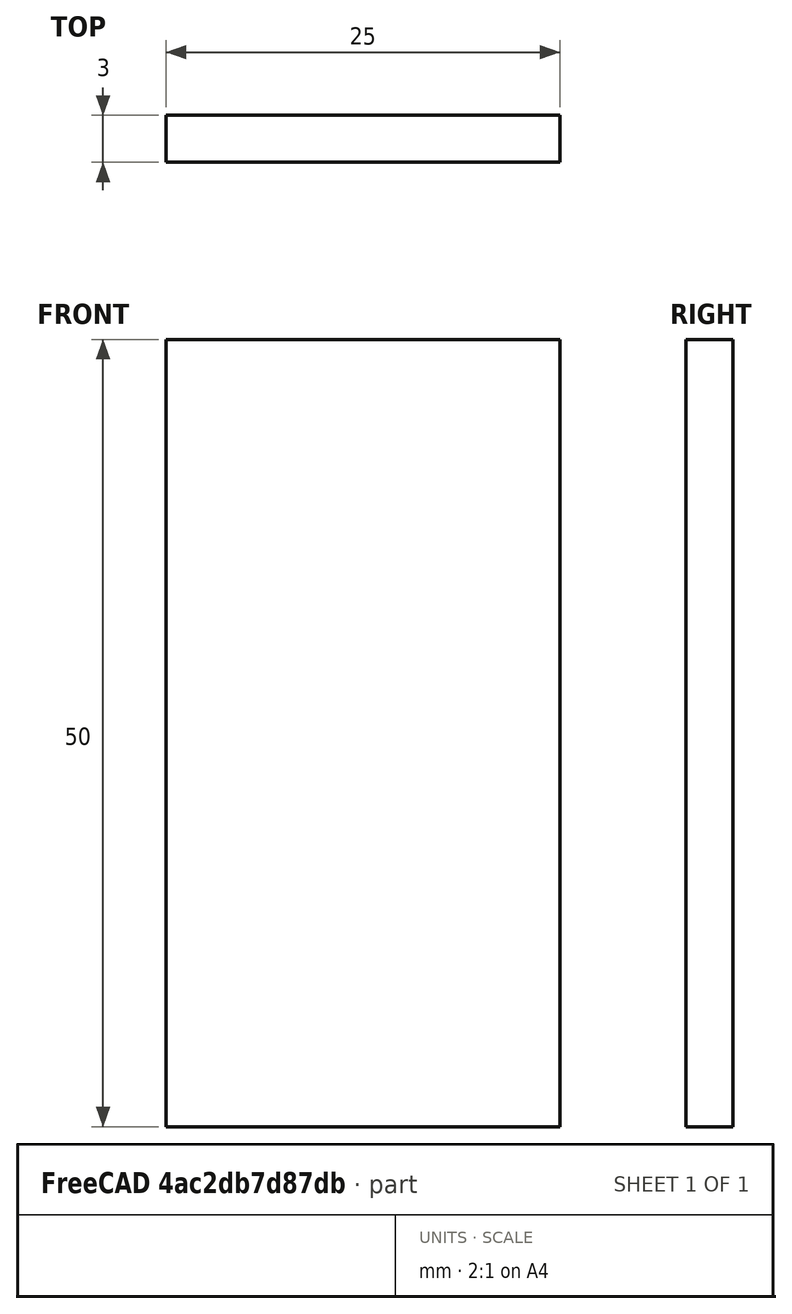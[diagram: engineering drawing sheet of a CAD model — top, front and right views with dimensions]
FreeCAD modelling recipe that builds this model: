
FCSTD DOCUMENT  (FreeCAD 0.15R4671 (Git))
Label: Flat Bar 25x3 EN10058 S235JR
License: All rights reserved
LicenseURL: http://en.wikipedia.org/wiki/All_rights_reserved
objects: Sketcher::SketchObject×1, Part::Extrusion×1
note: 2 computed .brp shape members not serialized (recipe doc carries the construction recipe); baked Part::Feature solids carry a one-line shape summary decoded from their .brp

FEATURE [Sketcher::SketchObject] Sketch
  sketch-geometry (4):
    g0: LineSegment StartX=-12.5 StartY=-1.5 StartZ=0 EndX=12.5 EndY=-1.5 EndZ=0
    g1: LineSegment StartX=12.5 StartY=-1.5 StartZ=0 EndX=12.5 EndY=1.5 EndZ=0
    g2: LineSegment StartX=12.5 StartY=1.5 StartZ=0 EndX=-12.5 EndY=1.5 EndZ=0
    g3: LineSegment StartX=-12.5 StartY=1.5 StartZ=0 EndX=-12.5 EndY=-1.5 EndZ=0
  constraints (12):
    c: Coincident(g0,g1)
    c: Coincident(g1,g2)
    c: Coincident(g2,g3)
    c: Coincident(g3,g0)
    c: Horizontal(g0)
    c: Horizontal(g2)
    c: Vertical(g1)
    c: Vertical(g3)
    c: Symmetric(g1,g2,g-2)
    c: Symmetric(g0,g1,g-1)
    c: DistanceY(g1) = 3
    c: DistanceX(g0) = 25
FEATURE [Part::Extrusion] Extrude  label="Flat Bar 25x3 EN10058 S235JR"
  Base = -> Sketch
  Dir = (0,0,50)
  Solid = true
